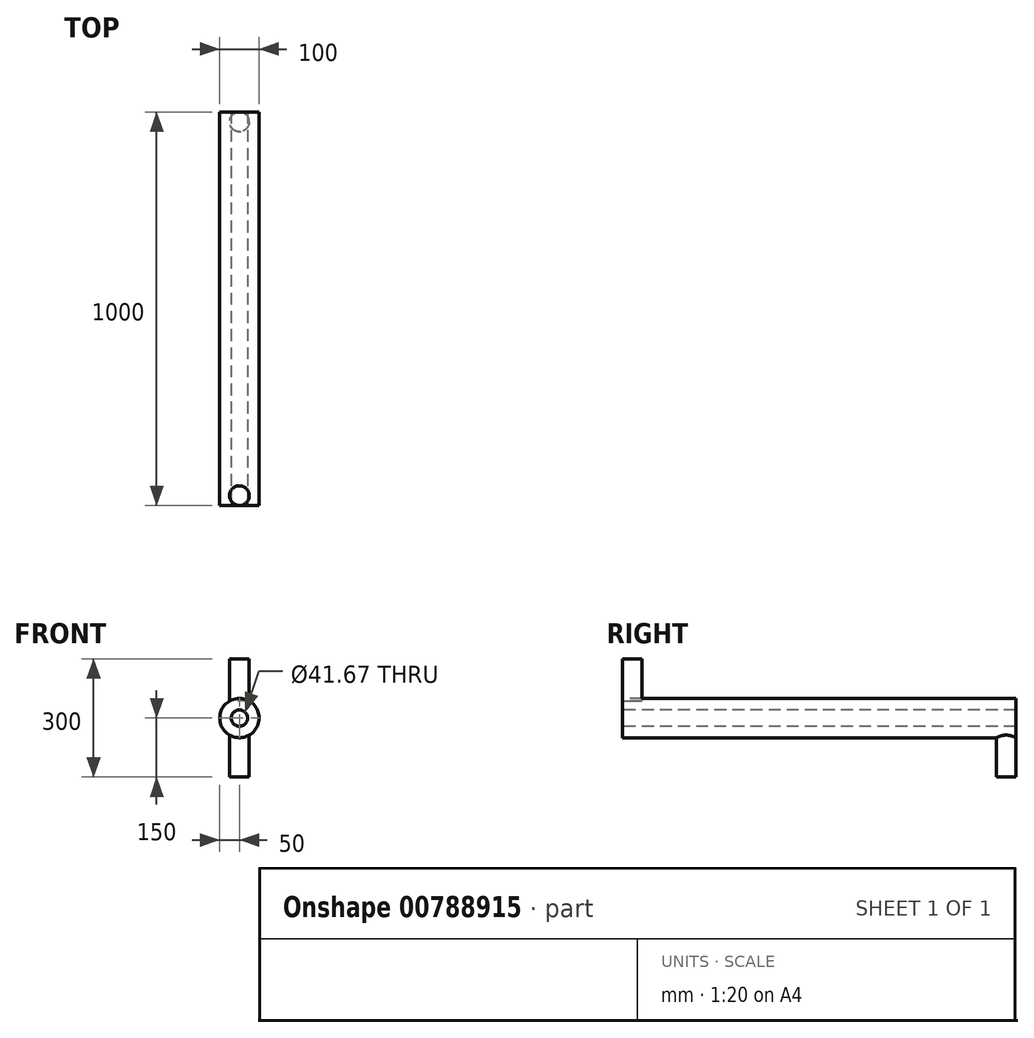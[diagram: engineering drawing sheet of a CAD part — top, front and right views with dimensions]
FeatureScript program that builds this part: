
annotation { "Feature Type Name" : "Feature", "Feature Type Description" : "" }
export const myFeature = defineFeature(function(context is Context, id is Id, definition is map)
    precondition{}
    {
        {
            var Q0;
            Q0=qCreatedBy(makeId("Front.planeOp"),FACE);
            var sketch = newSketch(context, id + "F0", { "sketchPlane" : qUnion([Q0])});
            skCircle(sketch, "E0", {"center": v(0, 0) * mm, "radius": 50 * mm});
            skCircle(sketch, "E1", {"center": v(0, 0) * mm, "radius": 20.83 * mm});
            skSolve(sketch);
        }
        {
            var Q0;
            Q0=makeQuery(id+"F0.imprint","IMPRINT",FACE,{"disambiguationData":[TD([[makeQuery(id+"F0.imprint","IMPRINT",EDGE,{"derivedFrom":sQuery(id+"F0.wireOp",EDGE,"E0")}),1.0]])]});
            var Q1;
            Q1 = qSketchRegion(id + "F5", true);
            var Q2;
            Q2=sQuery(id+"F0.wireOp",EDGE,"E0");
            extrude(context, id + "F1", {"entities" : qUnion([Q0, Q1]), "surfaceEntities" : qUnion([Q2]), "oppositeDirection" : true, "depth" : 1000 * mm, "offsetDistance" : 25 * mm});
        }
        {
            var Q0;
            Q0=qCreatedBy(makeId("Top.planeOp"),FACE);
            cPlane(context, id + "F2", {"entities" : qUnion([Q0]), "cplaneType" : CPlaneType.OFFSET, "offset" : 50 * mm, "width" : 150 * mm, "height" : 150 * mm});
        }
        {
            var Q0;
            Q0=qCreatedBy(id+"F2.planeOp",FACE);
            var sketch = newSketch(context, id + "F3", { "sketchPlane" : qUnion([Q0])});
            skCircle(sketch, "E2", {"center": v(0, 25) * mm, "radius": 25 * mm});
            skSolve(sketch);
        }
        {
            var Q0;
            Q0=qCreatedBy(makeId("Top.planeOp"),FACE);
            cPlane(context, id + "F4", {"entities" : qUnion([Q0]), "cplaneType" : CPlaneType.OFFSET, "offset" : 50 * mm, "oppositeDirection" : true, "width" : 150 * mm, "height" : 150 * mm});
        }
        {
            var Q0;
            Q0=qCreatedBy(id+"F4.planeOp",FACE);
            var sketch = newSketch(context, id + "F5", { "sketchPlane" : qUnion([Q0])});
            skCircle(sketch, "E3", {"center": v(0, 975) * mm, "radius": 25 * mm});
            skSolve(sketch);
        }
        {
            var Q0;
            Q0=makeQuery(id+"F5.imprint","IMPRINT",FACE,{"disambiguationData":[TD([[makeQuery(id+"F5.imprint","IMPRINT",EDGE,{"derivedFrom":sQuery(id+"F5.wireOp",EDGE,"E3")}),1.0]])]});
            extrude(context, id + "F6", {"entities" : qUnion([Q0]), "operationType" : NewBodyOperationType.ADD, "oppositeDirection" : true, "depth" : 100 * mm, "offsetDistance" : 25 * mm, "hasSecondDirection" : true, "secondDirectionOppositeDirection" : false, "secondDirectionDepth" : 7 * mm});
        }
        {
            var Q0;
            Q0=qSketchRegion(id+"F3",true);
            var Q1;
            Q1=sQuery(id+"F3.wireOp",EDGE,"E2");
            extrude(context, id + "F7", {"entities" : qUnion([Q0]), "surfaceEntities" : qUnion([Q1]), "oppositeDirection" : true, "depth" : 7 * mm, "offsetDistance" : 25 * mm, "hasSecondDirection" : true, "secondDirectionOppositeDirection" : false, "secondDirectionDepth" : 100 * mm});
        }
    });
